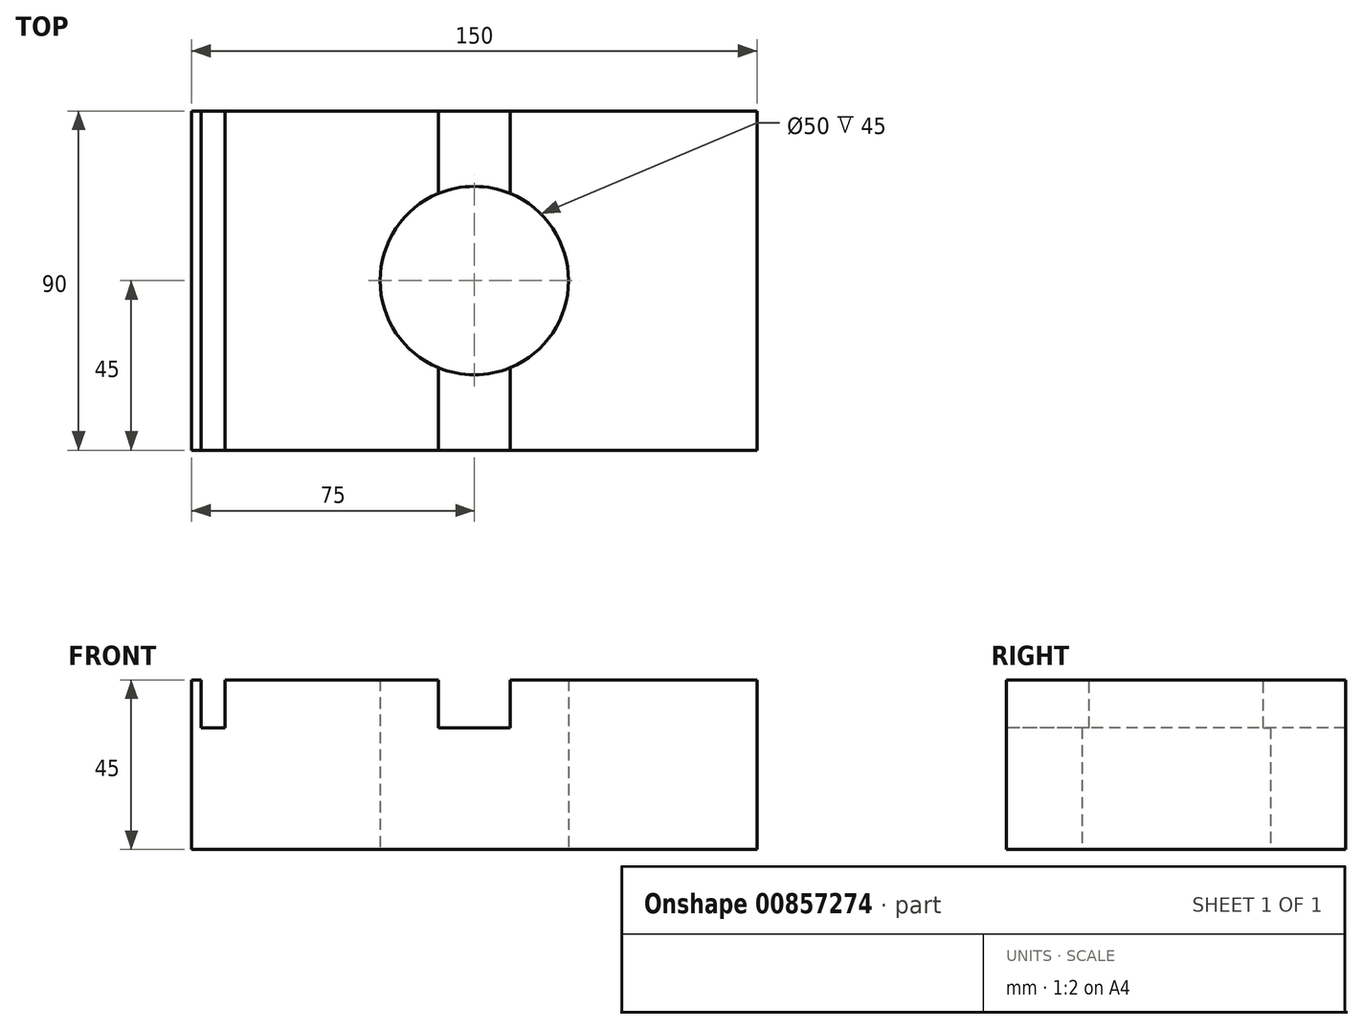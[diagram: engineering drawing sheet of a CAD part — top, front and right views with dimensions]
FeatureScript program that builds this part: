
annotation { "Feature Type Name" : "Feature", "Feature Type Description" : "" }
export const myFeature = defineFeature(function(context is Context, id is Id, definition is map)
    precondition{}
    {
        {
            var Q0;
            Q0=qCreatedBy(makeId("Top.planeOp"),FACE);
            var sketch = newSketch(context, id + "F0", { "sketchPlane" : qUnion([Q0])});
            skLineSegment(sketch, "E0.bottom", {"start": v(-75, 45) * mm, "end": v(75, 45) * mm});
            skLineSegment(sketch, "E0.top", {"start": v(-75, -45) * mm, "end": v(75, -45) * mm});
            skLineSegment(sketch, "E0.left", {"start": v(-75, 45) * mm, "end": v(-75, -45) * mm});
            skLineSegment(sketch, "E0.right", {"start": v(75, 45) * mm, "end": v(75, -45) * mm});
            skPoint(sketch, "E0.middle", {"position": v(0, 0) * mm});
            skCircle(sketch, "E1", {"center": v(0, 0) * mm, "radius": 25 * mm});
            skSolve(sketch);
        }
        {
            var Q0;
            Q0=makeQuery(id+"F0.imprint","IMPRINT",FACE,{"disambiguationData":[TD([[makeQuery(id+"F0.imprint","IMPRINT",EDGE,{"derivedFrom":sQuery(id+"F0.wireOp",EDGE,"E0.bottom")}),-1.0]])]});
            extrude(context, id + "F1", {"entities" : qUnion([Q0]), "depth" : 45 * mm, "offsetDistance" : 25.4 * mm});
        }
        {
            var Q0;
            Q0=makeQuery(id+"F1.opExtrude","CAP_FACE",FACE,{"disambiguationData":[OSD([sQuery(id+"F0.wireOp",EDGE,"E0.bottom"),sQuery(id+"F0.wireOp",EDGE,"E0.top"),sQuery(id+"F0.wireOp",EDGE,"E0.left"),sQuery(id+"F0.wireOp",EDGE,"E0.right"),sQuery(id+"F0.wireOp",EDGE,"E1")])],"isStart":false});
            var sketch = newSketch(context, id + "F2", { "sketchPlane" : qUnion([Q0])});
            skLineSegment(sketch, "E2.bottom", {"start": v(-72.46, 45) * mm, "end": v(-66.11, 45) * mm});
            skLineSegment(sketch, "E2.top", {"start": v(-72.46, -45) * mm, "end": v(-66.11, -45) * mm});
            skLineSegment(sketch, "E2.left", {"start": v(-72.46, 45) * mm, "end": v(-72.46, -45) * mm});
            skLineSegment(sketch, "E2.right", {"start": v(-66.11, 45) * mm, "end": v(-66.11, -45) * mm});
            skLineSegment(sketch, "E3", {"start": v(-9.52, 45) * mm, "end": v(-9.53, -45) * mm});
            skLineSegment(sketch, "E4", {"start": v(-9.53, -45) * mm, "end": v(9.53, -45) * mm});
            skLineSegment(sketch, "E5", {"start": v(9.53, -45) * mm, "end": v(9.53, 45) * mm});
            skLineSegment(sketch, "E6", {"start": v(9.52, 45) * mm, "end": v(-9.52, 45) * mm});
            skPoint(sketch, "E7", {"position": v(0, 0) * mm});
            skLineSegment(sketch, "E8", {"start": v(0, 45) * mm, "end": v(0, -45) * mm, "construction": true});
            skSolve(sketch);
        }
        {
            var Q0;
            Q0=makeQuery(id+"F2.imprint","IMPRINT",FACE,{"disambiguationData":[TD([[makeQuery(id+"F2.imprint","IMPRINT",EDGE,{"derivedFrom":sQuery(id+"F2.wireOp",EDGE,"E2.bottom")}),-1.0]])]});
            var Q1;
            {var subQ0=sQuery(id+"F2.wireOp",EDGE,"E4");Q1=makeQuery(id+"F2.imprint","IMPRINT",FACE,{"disambiguationData":[TD([[makeQuery(id+"F2.imprint","IMPRINT",EDGE,{"derivedFrom":subQ0}),1.0]])]});}
            var Q2;
            {var subQ0=sQuery(id+"F2.wireOp",EDGE,"E6");Q2=makeQuery(id+"F2.imprint","IMPRINT",FACE,{"disambiguationData":[TD([[makeQuery(id+"F2.imprint","IMPRINT",EDGE,{"derivedFrom":subQ0}),-1.0]])]});}
            var Q3;
            Q3 = qSketchRegion(id + "F5", true);
            extrude(context, id + "F3", {"entities" : qUnion([Q0, Q1, Q2, Q3]), "operationType" : NewBodyOperationType.REMOVE, "oppositeDirection" : true, "depth" : 12.7 * mm, "offsetDistance" : 25.4 * mm});
        }
    });
